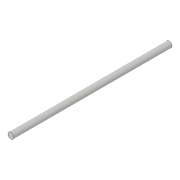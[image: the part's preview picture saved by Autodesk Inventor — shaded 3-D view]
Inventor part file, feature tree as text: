
AUTODESK INVENTOR PART (.ipt)
format: ipt  version: 2018.3 (Build 223284000, 284)  size: 69,632 bytes
history: native  units: in
note: dims shown in document units (in); Inventor stores cm internally (conversion verified against a paired STEP export)
features: extrude x1, sketch x1
ambient origin geometry x8: Origin, YZ Plane, XZ Plane, XY Plane, X Axis, Y Axis, Z Axis, Center Point
bodies: Solid1 (feature_tree)
feature tree (2):
  extrude  "Extrusion1"  Depth=5.0in TaperAngle=0.0deg
  sketch  "Sketch1"  dims[d0=0.1875in d1=5.0in d2=0.0in]
